# Revit family: 931-00-001 DN80-900
name_source: partatom
category: Pipe Accessories
units: mm (PartAtom-declared; Revit-internal decimal feet)

## family parameters
Always vertical = Yes
Cut with Voids When Loaded = No
Part Type = Valve - Breaks Into
Round Connector Dimension = Use Diameter
Shared = No
Work Plane-Based = No

## types (25) — shared parameters
1 = 1 mm  [stored 0.00328084 ft]
2 = 3 mm  [stored 0.00984252 ft]
DN080_PN10/16 = 931-080-00-020040200000
DN100_PN10/16 = 931-100-00-020040200000
DN150_PN10/16 = 931-150-00-020040200000
DN200_PN10 = 931-200-00-010020200000
DN200_PN16 = 931-200-00-020020200000
DN250 PN10 = 931-250-00-010020200000
DN250 PN16 = 931-250-00-020020200000
DN300_PN10 = 931-300-00-010020200000
DN300_PN16 = 931-300-00-020020200000
DN350_PN10 = 931-350-00-010020200000
DN350_PN16 = 931-350-00-020020200000
DN400_PN10 = 931-400-00-010020200000
DN400_PN16 = 931-400-00-020020200000
DN500_PN10 = 931-500-00-010020200000
DN500_PN16 = 931-500-00-020020200000
DN600_PN10 = 931-600-00-010020200000
DN600_PN16 = 931-600-00-020020200000
DN700_PN10 = 931-700-00-010020200000
DN700_PN16 = 931-700-00-020020200000
DN750_PN10 = 931-750-00-010020200000
DN750_PN16 = 931-750-00-020020200000
DN800_PN10 = 931-800-00-010020200000
DN800_PN16 = 931-800-00-020020200000
DN900_PN10 = 931-900-00-010020200000
DN900_PN16 = 931-900-00-020020200000
Description_ = AVK BUTTERFLY VALVE, FLANGED, PN10/16
Search_table = 931-00-001 DN80-900
URL_product_pages = https://www.avkvalves.com
zero-valued in all types: Default Elevation

## per-type parameters (varying)
| type | Actuator_FL_T | Actuator_Flange_R | B | B1 | Body_Thickness | Body_dim | Body_dim1 | Body_thickness | Bore_R | C | DN | E | F | Flange_R | Flange_T | G | H | PCD_R | disk | disk1 | disk2 | rubber |
| DN080_PN10/16 | 19 mm  [stored 0.062336 ft] | 45 mm  [stored 0.147638 ft] | 39 mm  [stored 0.127953 ft] | 40 mm  [stored 0.131234 ft] | 6 mm  [stored 0.019685 ft] | 34 mm | 39 mm  [stored 0.127953 ft] | 42 mm  [stored 0.137795 ft] | 40 mm  [stored 0.131234 ft] | 46 mm  [stored 0.150919 ft] | 80 mm | 159 mm | 18 mm  [stored 0.0590551 ft] | 97 mm | 19 mm  [stored 0.062336 ft] | 11 mm  [stored 0.0360892 ft] | 45 mm  [stored 0.147638 ft] | 77 mm | 4 mm  [stored 0.0131234 ft] | 10 mm  [stored 0.0328084 ft] | 78 mm | 29 mm |
| DN100_PN10/16 | 19 mm  [stored 0.062336 ft] | 45 mm  [stored 0.147638 ft] | 52 mm | 53 mm | 6 mm  [stored 0.019685 ft] | 34 mm | 44 mm | 56 mm | 50 mm | 52 mm | 100 mm | 178 mm | 22 mm  [stored 0.0721785 ft] | 110 mm | 19 mm  [stored 0.062336 ft] | 11 mm  [stored 0.0360892 ft] | 45 mm  [stored 0.147638 ft] | 90 mm | 6 mm  [stored 0.019685 ft] | 10 mm  [stored 0.0328084 ft] | 104 mm | 30 mm  [stored 0.0984252 ft] |
| DN150_PN10/16 | 19 mm  [stored 0.062336 ft] | 45 mm  [stored 0.147638 ft] | 74 mm | 75 mm | 6 mm  [stored 0.019685 ft] | 34 mm | 48 mm | 79 mm | 75 mm | 56 mm | 150 mm | 203 mm | 30 mm  [stored 0.0984252 ft] | 143 mm | 19 mm  [stored 0.062336 ft] | 14 mm  [stored 0.0459318 ft] | 45 mm  [stored 0.147638 ft] | 120 mm | 7 mm  [stored 0.0229659 ft] | 13 mm  [stored 0.0426509 ft] | 148 mm | 34 mm |
| DN200_PN10 | 19 mm  [stored 0.062336 ft] | 63 mm | 100 mm | 101 mm | 7 mm  [stored 0.0229659 ft] | 47 mm | 51 mm | 106 mm | 100 mm | 60 mm | 200 mm | 241 mm | 30 mm  [stored 0.0984252 ft] | 170 mm | 19 mm  [stored 0.062336 ft] | 17 mm  [stored 0.0557743 ft] | 63 mm | 148 mm | 9 mm  [stored 0.0295276 ft] | 15 mm  [stored 0.0492126 ft] | 199 mm | 35 mm  [stored 0.114829 ft] |
| DN200_PN16 | 20 mm  [stored 0.0656168 ft] | 63 mm | 100 mm | 101 mm | 7 mm  [stored 0.0229659 ft] | 47 mm | 51 mm | 106 mm | 100 mm | 60 mm | 200 mm | 241 mm | 30 mm  [stored 0.0984252 ft] | 170 mm | 20 mm  [stored 0.0656168 ft] | 17 mm  [stored 0.0557743 ft] | 63 mm | 148 mm | 9 mm  [stored 0.0295276 ft] | 15 mm  [stored 0.0492126 ft] | 199 mm | 35 mm  [stored 0.114829 ft] |
| DN250 PN10 | 22 mm  [stored 0.0721785 ft] | 63 mm | 125 mm | 126 mm | 8 mm  [stored 0.0262467 ft] | 47 mm | 58 mm | 132 mm | 125 mm | 68 mm | 250 mm | 273 mm | 32 mm  [stored 0.104987 ft] | 200 mm | 22 mm  [stored 0.0721785 ft] | 22 mm  [stored 0.0721785 ft] | 75 mm | 175 mm | 11 mm  [stored 0.0360892 ft] | 20 mm  [stored 0.0656168 ft] | 250 mm | 38 mm |
| DN250 PN16 | 20 mm  [stored 0.0656168 ft] | 63 mm | 125 mm | 126 mm | 8 mm  [stored 0.0262467 ft] | 47 mm | 58 mm | 132 mm | 125 mm | 68 mm | 250 mm | 273 mm | 32 mm  [stored 0.104987 ft] | 200 mm | 20 mm  [stored 0.0656168 ft] | 22 mm  [stored 0.0721785 ft] | 75 mm | 178 mm | 11 mm  [stored 0.0360892 ft] | 20 mm  [stored 0.0656168 ft] | 250 mm | 38 mm |
| DN300_PN10 | 20 mm  [stored 0.0656168 ft] | 63 mm | 150 mm | 151 mm | 8 mm  [stored 0.0262467 ft] | 47 mm | 66 mm | 159 mm | 150 mm | 78 mm | 300 mm | 311 mm | 32 mm  [stored 0.104987 ft] | 228 mm | 25 mm  [stored 0.082021 ft] | 22 mm  [stored 0.0721785 ft] | 75 mm | 200 mm | 11 mm  [stored 0.0360892 ft] | 20 mm  [stored 0.0656168 ft] | 300 mm | 39 mm  [stored 0.127953 ft] |
| DN300_PN16 | 20 mm  [stored 0.0656168 ft] | 63 mm | 150 mm | 151 mm | 8 mm  [stored 0.0262467 ft] | 47 mm | 66 mm | 159 mm | 150 mm | 78 mm | 300 mm | 311 mm | 32 mm  [stored 0.104987 ft] | 228 mm | 25 mm  [stored 0.082021 ft] | 22 mm  [stored 0.0721785 ft] | 75 mm | 205 mm | 11 mm  [stored 0.0360892 ft] | 20 mm  [stored 0.0656168 ft] | 300 mm | 39 mm  [stored 0.127953 ft] |
| DN350_PN10 | 20 mm  [stored 0.0656168 ft] | 75 mm | 174 mm | 175 mm | 2 mm  [stored 0.00656168 ft] | 56 mm | 66 mm | 184 mm | 175 mm | 78 mm | 350 mm | 306 mm | 32 mm  [stored 0.104987 ft] | 200 mm | 25 mm  [stored 0.082021 ft] | 27 mm  [stored 0.0885827 ft] | 88 mm | 230 mm | 14 mm  [stored 0.0459318 ft] | 24 mm | 348 mm | 13 mm  [stored 0.0426509 ft] |
| DN350_PN16 | 20 mm  [stored 0.0656168 ft] | 75 mm | 174 mm | 175 mm | 2 mm  [stored 0.00656168 ft] | 56 mm | 66 mm | 184 mm | 175 mm | 78 mm | 350 mm | 306 mm | 32 mm  [stored 0.104987 ft] | 200 mm | 27 mm  [stored 0.0885827 ft] | 27 mm  [stored 0.0885827 ft] | 88 mm | 235 mm | 14 mm  [stored 0.0459318 ft] | 24 mm | 348 mm | 13 mm  [stored 0.0426509 ft] |
| DN400_PN10 | 20 mm  [stored 0.0656168 ft] | 75 mm | 195 mm | 196 mm | 2 mm  [stored 0.00656168 ft] | 56 mm | 87 mm | 206 mm | 200 mm | 102 mm | 400 mm | 328 mm | 43 mm  [stored 0.141076 ft] | 228 mm | 25 mm  [stored 0.082021 ft] | 27 mm  [stored 0.0885827 ft] | 88 mm | 258 mm | 14 mm  [stored 0.0459318 ft] | 24 mm | 390 mm | 14 mm  [stored 0.0459318 ft] |
| DN400_PN16 | 20 mm  [stored 0.0656168 ft] | 75 mm | 195 mm | 196 mm | 2 mm  [stored 0.00656168 ft] | 56 mm | 87 mm | 206 mm | 200 mm | 102 mm | 400 mm | 328 mm | 43 mm  [stored 0.141076 ft] | 230 mm | 28 mm  [stored 0.0918635 ft] | 27 mm  [stored 0.0885827 ft] | 88 mm | 263 mm | 14 mm  [stored 0.0459318 ft] | 24 mm | 390 mm | 15 mm  [stored 0.0492126 ft] |
| DN500_PN10 | 20 mm  [stored 0.0656168 ft] | 88 mm | 246 mm | 247 mm | 2 mm  [stored 0.00656168 ft] | 66 mm | 108 mm | 259 mm | 250 mm | 127 mm | 500 mm | 403 mm | 39 mm  [stored 0.127953 ft] | 285 mm | 27 mm  [stored 0.0885827 ft] | 36 mm  [stored 0.11811 ft] | 105 mm | 310 mm | 18 mm  [stored 0.0590551 ft] | 32 mm  [stored 0.104987 ft] | 492 mm | 18 mm  [stored 0.0590551 ft] |
| DN500_PN16 | 18 mm  [stored 0.0590551 ft] | 88 mm | 246 mm | 247 mm | 2 mm  [stored 0.00656168 ft] | 66 mm | 108 mm | 259 mm | 250 mm | 127 mm | 500 mm | 403 mm | 39 mm  [stored 0.127953 ft] | 300 mm | 32 mm  [stored 0.104987 ft] | 36 mm  [stored 0.11811 ft] | 105 mm | 325 mm | 18 mm  [stored 0.0590551 ft] | 32 mm  [stored 0.104987 ft] | 492 mm | 25 mm  [stored 0.082021 ft] |
| DN600_PN10 | 30 mm  [stored 0.0984252 ft] | 105 mm | 289 mm | 290 mm | 2 mm  [stored 0.00656168 ft] | 79 mm | 131 mm | 304 mm | 300 mm | 154 mm | 600 mm | 495 mm | 68 mm | 350 mm | 30 mm  [stored 0.0984252 ft] | 46 mm  [stored 0.150919 ft] | 105 mm | 363 mm | 23 mm  [stored 0.0754593 ft] | 41 mm | 577 mm | 25 mm  [stored 0.082021 ft] |
| DN600_PN16 | 30 mm  [stored 0.0984252 ft] | 105 mm | 289 mm | 290 mm | 2 mm  [stored 0.00656168 ft] | 79 mm | 131 mm | 304 mm | 300 mm | 154 mm | 600 mm | 495 mm | 68 mm | 350 mm | 36 mm  [stored 0.11811 ft] | 46 mm  [stored 0.150919 ft] | 105 mm | 385 mm | 23 mm  [stored 0.0754593 ft] | 41 mm | 577 mm | 25 mm  [stored 0.082021 ft] |
| DN700_PN10 | 30 mm  [stored 0.0984252 ft] | 105 mm | 341 mm | 342 mm | 2 mm  [stored 0.00656168 ft] | 79 mm | 140 mm | 359 mm | 350 mm | 165 mm | 700 mm | 565 mm | 68 mm | 410 mm | 33 mm | 46 mm  [stored 0.150919 ft] | 105 mm | 420 mm | 23 mm  [stored 0.0754593 ft] | 41 mm | 681 mm | 30 mm  [stored 0.0984252 ft] |
| DN700_PN16 | 30 mm  [stored 0.0984252 ft] | 105 mm | 341 mm | 342 mm | 2 mm  [stored 0.00656168 ft] | 79 mm | 140 mm | 359 mm | 350 mm | 165 mm | 700 mm | 565 mm | 68 mm | 410 mm | 40 mm  [stored 0.131234 ft] | 46 mm  [stored 0.150919 ft] | 105 mm | 420 mm | 23 mm  [stored 0.0754593 ft] | 41 mm | 681 mm | 30 mm  [stored 0.0984252 ft] |
| DN750_PN10 | 30 mm  [stored 0.0984252 ft] | 105 mm | 372 mm | 373 mm | 2 mm  [stored 0.00656168 ft] | 79 mm | 140 mm | 391 mm | 375 mm | 165 mm | 750 mm | 584 mm | 68 mm | 430 mm | 40 mm  [stored 0.131234 ft] | 46 mm  [stored 0.150919 ft] | 105 mm | 420 mm | 23 mm  [stored 0.0754593 ft] | 41 mm | 743 mm | 28 mm  [stored 0.0918635 ft] |
| DN750_PN16 | 30 mm  [stored 0.0984252 ft] | 105 mm | 372 mm | 373 mm | 2 mm  [stored 0.00656168 ft] | 79 mm | 140 mm | 391 mm | 375 mm | 165 mm | 750 mm | 584 mm | 68 mm | 425 mm | 40 mm  [stored 0.131234 ft] | 46 mm  [stored 0.150919 ft] | 105 mm | 420 mm | 23 mm  [stored 0.0754593 ft] | 41 mm | 743 mm | 25 mm  [stored 0.082021 ft] |
| DN800_PN10 | 32 mm  [stored 0.104987 ft] | 150 mm | 394 mm | 395 mm | 2 mm  [stored 0.00656168 ft] | 113 mm | 162 mm | 414 mm | 400 mm | 190 mm | 800 mm | 645 mm | 75 mm | 460 mm | 35 mm  [stored 0.114829 ft] | 55 mm | 150 mm | 475 mm | 28 mm  [stored 0.0918635 ft] | 50 mm | 787 mm | 30 mm  [stored 0.0984252 ft] |
| DN800_PN16 | 32 mm  [stored 0.104987 ft] | 150 mm | 394 mm | 395 mm | 2 mm  [stored 0.00656168 ft] | 113 mm | 162 mm | 414 mm | 400 mm | 190 mm | 800 mm | 645 mm | 75 mm | 465 mm | 43 mm  [stored 0.141076 ft] | 55 mm | 150 mm | 475 mm | 28 mm  [stored 0.0918635 ft] | 50 mm | 787 mm | 33 mm |
| DN900_PN10 | 35 mm  [stored 0.114829 ft] | 150 mm | 450 mm | 451 mm | 2 mm  [stored 0.00656168 ft] | 113 mm | 170 mm | 473 mm | 450 mm | 200 mm | 900 mm | 705 mm | 75 mm | 520 mm | 38 mm | 55 mm | 150 mm | 525 mm | 28 mm  [stored 0.0918635 ft] | 50 mm | 899 mm | 35 mm  [stored 0.114829 ft] |
| DN900_PN16 | 35 mm  [stored 0.114829 ft] | 150 mm | 450 mm | 451 mm | 2 mm  [stored 0.00656168 ft] | 113 mm | 170 mm | 473 mm | 450 mm | 200 mm | 900 mm | 705 mm | 75 mm | 525 mm | 47 mm | 55 mm | 150 mm | 525 mm | 28 mm  [stored 0.0918635 ft] | 50 mm | 899 mm | 38 mm |

note: [stored X ft] marks values corroborated as IEEE doubles in the binary element streams (Revit-internal decimal feet)

## geometry (parser evidence)
native form markers: Sweep x7
no freeform markers — native parametric forms only
